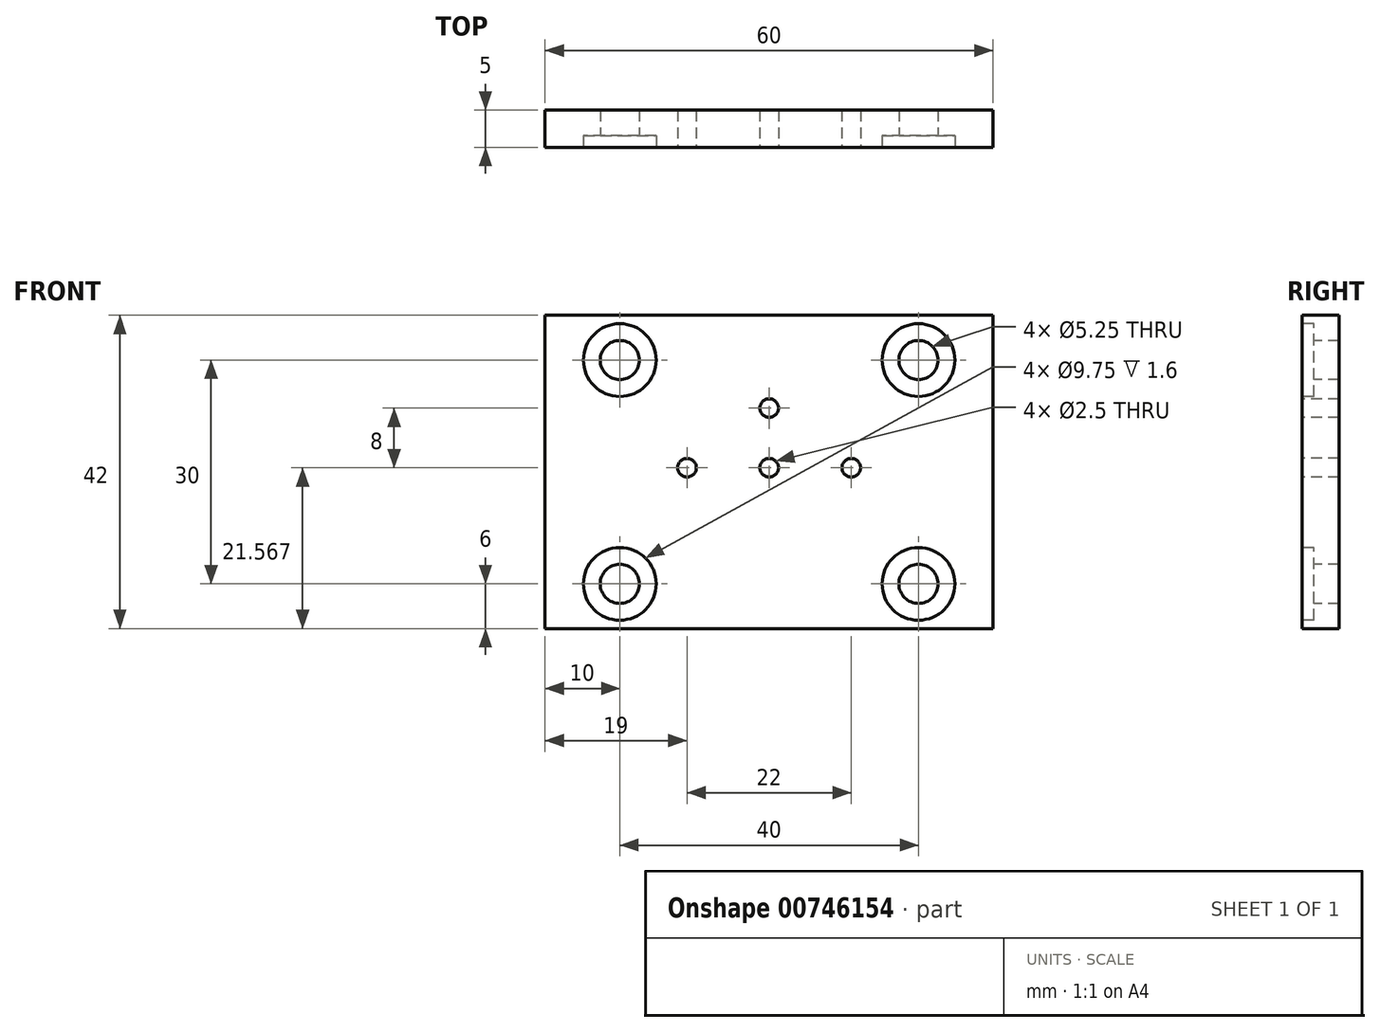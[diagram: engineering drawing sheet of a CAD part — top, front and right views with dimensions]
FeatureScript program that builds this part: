
annotation { "Feature Type Name" : "Feature", "Feature Type Description" : "" }
export const myFeature = defineFeature(function(context is Context, id is Id, definition is map)
    precondition{}
    {
        {
            var Q0;
            Q0=qCreatedBy(makeId("Front.planeOp"),FACE);
            var sketch = newSketch(context, id + "F0", { "sketchPlane" : qUnion([Q0])});
            skLineSegment(sketch, "E0.bottom", {"start": v(-18.5, 0) * mm, "end": v(18.5, 0) * mm});
            skLineSegment(sketch, "E0.top", {"start": v(-18.5, -42) * mm, "end": v(18.5, -42) * mm});
            skLineSegment(sketch, "E0.left", {"start": v(-18.5, 0) * mm, "end": v(-18.5, -42) * mm});
            skLineSegment(sketch, "E0.right", {"start": v(18.5, 0) * mm, "end": v(18.5, -42) * mm});
            skLineSegment(sketch, "E1.bottom", {"start": v(-18.5, -42) * mm, "end": v(-30, -42) * mm});
            skLineSegment(sketch, "E1.top", {"start": v(-18.5, 0) * mm, "end": v(-30, 0) * mm});
            skLineSegment(sketch, "E1.left", {"start": v(-18.5, -42) * mm, "end": v(-18.5, 0) * mm});
            skLineSegment(sketch, "E1.right", {"start": v(-30, -42) * mm, "end": v(-30, 0) * mm});
            skLineSegment(sketch, "E2.bottom", {"start": v(18.5, 0) * mm, "end": v(30, 0) * mm});
            skLineSegment(sketch, "E2.top", {"start": v(18.5, -42) * mm, "end": v(30, -42) * mm});
            skLineSegment(sketch, "E2.right", {"start": v(30, 0) * mm, "end": v(30, -42) * mm});
            skSolve(sketch);
        }
        {
            var Q0;
            Q0=makeQuery(id+"F0.imprint","IMPRINT",FACE,{"disambiguationData":[TD([[makeQuery(id+"F0.imprint","IMPRINT",EDGE,{"derivedFrom":sQuery(id+"F0.wireOp",EDGE,"E1.bottom")}),-1.0]])]});
            var Q1;
            Q1=makeQuery(id+"F0.imprint","IMPRINT",FACE,{"disambiguationData":[TD([[makeQuery(id+"F0.imprint","IMPRINT",EDGE,{"derivedFrom":sQuery(id+"F0.wireOp",EDGE,"E0.bottom")}),-1.0]])]});
            var Q2;
            Q2=makeQuery(id+"F0.imprint","IMPRINT",FACE,{"disambiguationData":[TD([[makeQuery(id+"F0.imprint","IMPRINT",EDGE,{"derivedFrom":sQuery(id+"F0.wireOp",EDGE,"E2.bottom")}),-1.0]])]});
            extrude(context, id + "F1", {"entities" : qUnion([Q0, Q1, Q2]), "depth" : 5 * mm, "offsetDistance" : 25 * mm});
        }
        {
            var Q0;
            Q0=makeQuery(id+"F1.opExtrude","CAP_FACE",FACE,{"disambiguationData":[OSD([sQuery(id+"F0.wireOp",EDGE,"E0.bottom"),sQuery(id+"F0.wireOp",EDGE,"E0.top"),sQuery(id+"F0.wireOp",EDGE,"E1.bottom"),sQuery(id+"F0.wireOp",EDGE,"E1.top"),sQuery(id+"F0.wireOp",EDGE,"E1.right"),sQuery(id+"F0.wireOp",EDGE,"E2.bottom"),sQuery(id+"F0.wireOp",EDGE,"E2.top"),sQuery(id+"F0.wireOp",EDGE,"E2.right")])],"isStart":false});
            var sketch = newSketch(context, id + "F2", { "sketchPlane" : qUnion([Q0])});
            skPoint(sketch, "E3", {"position": v(-20, -6) * mm});
            skPoint(sketch, "E4", {"position": v(20, -6) * mm});
            skPoint(sketch, "E5", {"position": v(20, -36) * mm});
            skPoint(sketch, "E6", {"position": v(-20, -36) * mm});
            skLineSegment(sketch, "E7", {"start": v(-20, -6) * mm, "end": v(-30, -6) * mm, "construction": true});
            skLineSegment(sketch, "E8", {"start": v(-20, -36) * mm, "end": v(-30, -36) * mm, "construction": true});
            skLineSegment(sketch, "E9", {"start": v(20, -36) * mm, "end": v(30, -36) * mm, "construction": true});
            skLineSegment(sketch, "E10", {"start": v(20, -6) * mm, "end": v(30, -6) * mm, "construction": true});
            skPoint(sketch, "E11", {"position": v(11, -20.43) * mm});
            skPoint(sketch, "E12", {"position": v(0, -20.43) * mm});
            skPoint(sketch, "E13", {"position": v(-11, -20.43) * mm});
            skPoint(sketch, "E14", {"position": v(0, -12.43) * mm});
            skLineSegment(sketch, "E15", {"start": v(-30, -12.43) * mm, "end": v(30, -12.43) * mm, "construction": true});
            skLineSegment(sketch, "E16", {"start": v(30, -20.43) * mm, "end": v(-19, -20.43) * mm, "construction": true});
            skLineSegment(sketch, "E17", {"start": v(0, -12.43) * mm, "end": v(0, -20.43) * mm});
            skLineSegment(sketch, "E18", {"start": v(11, -20.43) * mm, "end": v(0, -12.43) * mm});
            skLineSegment(sketch, "E19", {"start": v(-11, -20.43) * mm, "end": v(0, -12.43) * mm});
            skLineSegment(sketch, "E20", {"start": v(0, -20.43) * mm, "end": v(-11, -20.43) * mm});
            skLineSegment(sketch, "E21", {"start": v(0, -20.43) * mm, "end": v(11, -20.43) * mm});
            skSolve(sketch);
        }
        {
            var Q0;
            Q0=sQuery(id+"F2.wireOp",VERTEX,"E3");
            var Q1;
            Q1=sQuery(id+"F2.wireOp",VERTEX,"E4");
            var Q2;
            Q2=sQuery(id+"F2.wireOp",VERTEX,"E5");
            var Q3;
            Q3=sQuery(id+"F2.wireOp",VERTEX,"E6");
            var Q4;
            Q4=makeQuery(id+"F1.opExtrude","SWEPT_BODY",BODY,{"disambiguationData":[OSD([sQuery(id+"F0.wireOp",EDGE,"E0.bottom"),sQuery(id+"F0.wireOp",EDGE,"E0.top"),sQuery(id+"F0.wireOp",EDGE,"E1.bottom"),sQuery(id+"F0.wireOp",EDGE,"E1.top"),sQuery(id+"F0.wireOp",EDGE,"E1.right"),sQuery(id+"F0.wireOp",EDGE,"E2.bottom"),sQuery(id+"F0.wireOp",EDGE,"E2.top"),sQuery(id+"F0.wireOp",EDGE,"E2.right")])]});
            hole(context, id + "F3", {"style" : HoleStyle.C_BORE, "endStyle" : HoleEndStyle.BLIND, "holeDiameter" : 5.25 * mm, "cBoreDiameter" : 9.75 * mm, "cBoreDepth" : 1.6 * mm, "majorDiameter" : 5 * mm, "holeDepth" : 50 * mm, "isTappedThrough" : true, "tappedDepth" : 12 * mm, "tapClearance" : 3, "startFromSketch" : true, "locations" : qUnion([Q0, Q1, Q2, Q3]), "scope" : qUnion([Q4])});
        }
        {
            var Q0;
            Q0=sQuery(id+"F2.wireOp",VERTEX,"E14");
            var Q1;
            Q1=sQuery(id+"F2.wireOp",VERTEX,"E12");
            var Q2;
            Q2=sQuery(id+"F2.wireOp",VERTEX,"E13");
            var Q3;
            Q3=sQuery(id+"F2.wireOp",VERTEX,"E11");
            var Q4;
            Q4=makeQuery(id+"F1.opExtrude","SWEPT_BODY",BODY,{"disambiguationData":[OSD([sQuery(id+"F0.wireOp",EDGE,"E0.bottom"),sQuery(id+"F0.wireOp",EDGE,"E0.top"),sQuery(id+"F0.wireOp",EDGE,"E1.bottom"),sQuery(id+"F0.wireOp",EDGE,"E1.top"),sQuery(id+"F0.wireOp",EDGE,"E1.right"),sQuery(id+"F0.wireOp",EDGE,"E2.bottom"),sQuery(id+"F0.wireOp",EDGE,"E2.top"),sQuery(id+"F0.wireOp",EDGE,"E2.right")])]});
            hole(context, id + "F4", {"style" : HoleStyle.SIMPLE, "endStyle" : HoleEndStyle.THROUGH, "standardTappedOrClearance" : lookupTablePath({ "standard" : "ISO", "engagement" : "75%", "pitch" : "0.5 mm", "size" : "M3", "type" : "Tapped" }), "standardBlindInLast" : lookupTablePath({ "standard" : "ISO", "engagement" : "75%", "pitch" : "0.5 mm", "size" : "M3", "type" : "Tapped" }), "holeDiameter" : 2.5 * mm, "majorDiameter" : 3 * mm, "showTappedDepth" : true, "isTappedThrough" : true, "tappedDepth" : 12 * mm, "tapClearance" : 3, "startFromSketch" : true, "locations" : qUnion([Q0, Q1, Q2, Q3]), "scope" : qUnion([Q4])});
        }
    });
